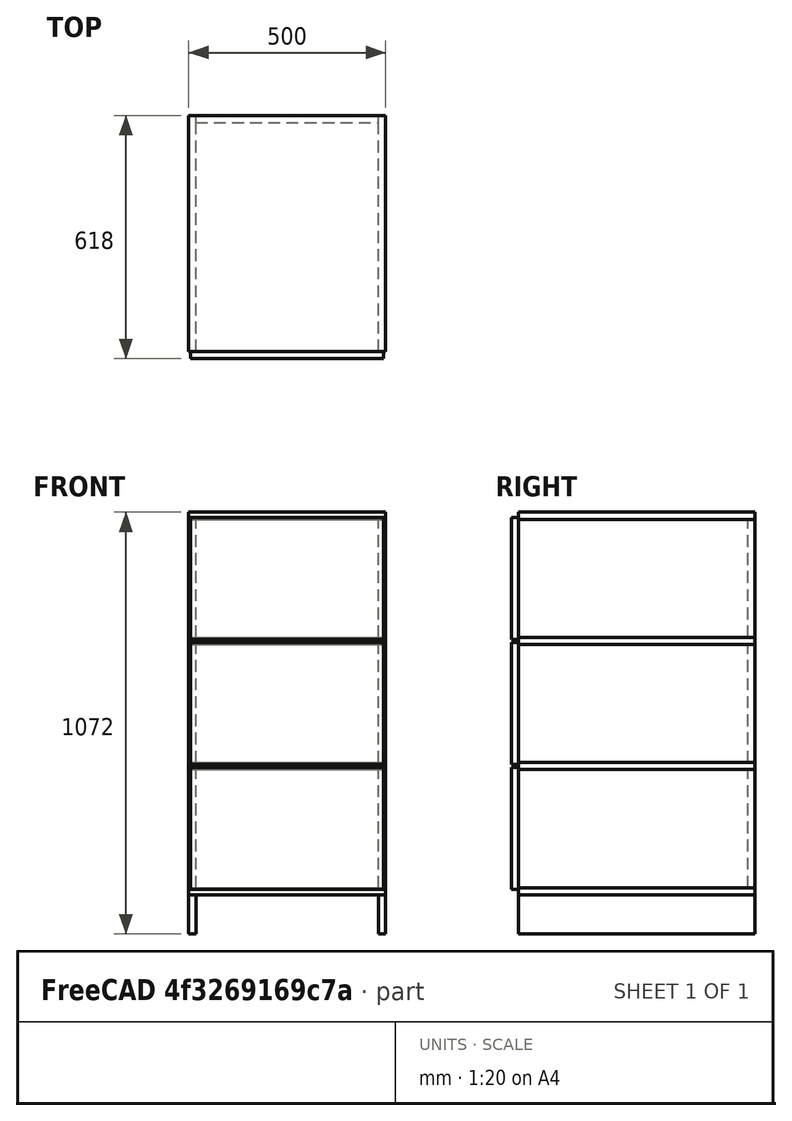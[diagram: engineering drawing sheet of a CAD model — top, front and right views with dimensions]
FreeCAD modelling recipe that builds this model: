
FCSTD DOCUMENT  (FreeCAD 0.21R33771 (Git))
Label: Test002_edgeband
License: All rights reserved
LicenseURL: http://en.wikipedia.org/wiki/All_rights_reserved
objects: Part::Box×18, App::DocumentObjectGroup×7, Spreadsheet::Sheet×1, TechDraw::DrawSVGTemplate×1, TechDraw::DrawViewSpreadsheet×1, TechDraw::DrawPage×1
note: 18 computed .brp shape members not serialized (recipe doc carries the construction recipe); baked Part::Feature solids carry a one-line shape summary decoded from their .brp

FEATURE [Part::Box] Box006  label="Foot L"
  AttacherType = Attacher::AttachEngine3D
  Height = 100
  Length = 18
  Width = 600
FEATURE [Part::Box] Box007  label="Side L1"
  AttacherType = Attacher::AttachEngine3D
  Height = 300
  Length = 18
  Placement = pos=(0,0,118) rot=(0,0,1;0rad)
  Width = 600
FEATURE [Part::Box] Box008  label="Side L2"
  AttacherType = Attacher::AttachEngine3D
  Height = 300
  Length = 18
  Placement = pos=(0,0,436) rot=(0,0,1;0rad)
  Width = 600
FEATURE [Part::Box] Box009  label="Side L3"
  AttacherType = Attacher::AttachEngine3D
  Height = 300
  Length = 18
  Placement = pos=(0,0,754) rot=(0,0,1;0rad)
  Width = 600
FEATURE [Part::Box] Box010  label="Foot R"
  AttacherType = Attacher::AttachEngine3D
  Height = 100
  Length = 18
  Placement = pos=(482,0,0) rot=(0,0,1;0rad)
  Width = 600
FEATURE [Part::Box] Box011  label="Side R1"
  AttacherType = Attacher::AttachEngine3D
  Height = 300
  Length = 18
  Placement = pos=(482,0,118) rot=(0,0,1;0rad)
  Width = 600
FEATURE [Part::Box] Box012  label="Side R2"
  AttacherType = Attacher::AttachEngine3D
  Height = 300
  Length = 18
  Placement = pos=(482,0,436) rot=(0,0,1;0rad)
  Width = 600
FEATURE [Part::Box] Box013  label="Side R3"
  AttacherType = Attacher::AttachEngine3D
  Height = 300
  Length = 18
  Placement = pos=(482,0,754) rot=(0,0,1;0rad)
  Width = 600
FEATURE [Part::Box] Box018  label="Back 1"
  AttacherType = Attacher::AttachEngine3D
  Height = 300
  Length = 464
  Placement = pos=(18,582,118) rot=(0,0,1;0rad)
  Width = 18
FEATURE [Part::Box] Box019  label="Back 2"
  AttacherType = Attacher::AttachEngine3D
  Height = 300
  Length = 464
  Placement = pos=(18,582,436) rot=(0,0,1;0rad)
  Width = 18
FEATURE [Part::Box] Box020  label="Back 3"
  AttacherType = Attacher::AttachEngine3D
  Height = 300
  Length = 464
  Placement = pos=(18,582,754) rot=(0,0,1;0rad)
  Width = 18
FEATURE [Part::Box] Box023  label="Top 1"
  AttacherType = Attacher::AttachEngine3D
  Height = 18
  Length = 500
  Placement = pos=(0,0,100) rot=(0,0,1;0rad)
  Width = 600
FEATURE [Part::Box] Box024  label="Top 2"
  AttacherType = Attacher::AttachEngine3D
  Height = 18
  Length = 500
  Placement = pos=(0,0,418) rot=(0,0,1;0rad)
  Width = 600
FEATURE [Part::Box] Box025  label="Top 3"
  AttacherType = Attacher::AttachEngine3D
  Height = 18
  Length = 500
  Placement = pos=(0,0,736) rot=(0,0,1;0rad)
  Width = 600
FEATURE [Part::Box] Box026  label="Top 4"
  AttacherType = Attacher::AttachEngine3D
  Height = 18
  Length = 500
  Placement = pos=(0,0,1054) rot=(0,0,1;0rad)
  Width = 600
FEATURE [Part::Box] Box027  label="Front 1"
  AttacherType = Attacher::AttachEngine3D
  Height = 310
  Length = 490
  Placement = pos=(5,-18,113) rot=(0,0,1;0rad)
  Width = 18
FEATURE [Part::Box] Box028  label="Front 2"
  AttacherType = Attacher::AttachEngine3D
  Height = 310
  Length = 490
  Placement = pos=(5,-18,431) rot=(0,0,1;0rad)
  Width = 18
FEATURE [Part::Box] Box029  label="Front 3"
  AttacherType = Attacher::AttachEngine3D
  Height = 310
  Length = 490
  Placement = pos=(5,-18,749) rot=(0,0,1;0rad)
  Width = 18
FEATURE [App::DocumentObjectGroup] Group006  label="Front"
  Group = -> [Box027,Box028,Box029]
FEATURE [App::DocumentObjectGroup] Group005  label="Top"
  Group = -> [Box023,Box024,Box025,Box026]
FEATURE [App::DocumentObjectGroup] Group004  label="Back"
  Group = -> [Box018,Box019,Box020]
FEATURE [App::DocumentObjectGroup] Group003  label="Side"
  Group = -> [Box007,Box008,Box009,Box011,Box012,Box013]
FEATURE [App::DocumentObjectGroup] Group007  label="Foot"
  Group = -> [Box006,Box010]
FEATURE [App::DocumentObjectGroup] Group002  label="White"
  Group = -> [Group003,Group004,Group005,Group006,Group007]
FEATURE [App::DocumentObjectGroup] Group001  label="Parts"
  Group = -> [Group002]
FEATURE [Spreadsheet::Sheet] toCut
  cells = A1='Name; B1='Dimensions; E1='Thickness; F1='Quantity; G1='m2; A2='Foot L; B2='100 mm; C2='x; D2='600 mm; E2='18 mm; F2=1; G2='0.06; A3=5; B3=6; D3=1; E3=2; F3=3; G3=4; A4='edge; F4='edge; G4='edge; A5='600 mm; F5='100 mm; G5='100 mm; A6='black; F6='black; G6='black; A8='Name; B8='Dimensions; E8='Thickness; F8='Quantity; G8='m2; A9='Side L1; B9='300 mm; C9='x; D9='600 mm; E9='18 mm; F9=1; G9='0.18; A10=5; B10=6; D10=1; E10=2; F10=3; G10=4; F11='edge; G11='edge; F12='300 mm; G12='300 mm; F13='black; G13='black; A15='Name; B15='Dimensions; E15='Thickness; F15='Quantity; G15='m2; A16='Side L2; B16='300 mm; C16='x; D16='600 mm; E16='18 mm; F16=1; G16='0.18; A17=5; B17=6; D17=1; E17=2; F17=3; G17=4; F18='edge; G18='edge; F19='300 mm; G19='300 mm; F20='black; G20='black; A22='Name; B22='Dimensions; E22='Thickness; F22='Quantity; G22='m2; A23='Side L3; B23='300 mm; C23='x; D23='600 mm; E23='18 mm; F23=1; G23='0.18; A24=5; B24=6; D24=1; E24=2; F24=3; G24=4; F25='edge; G25='edge; F26='300 mm; G26='300 mm; F27='black; G27='black; A29='Name; B29='Dimensions; E29='Thickness; F29='Quantity; G29='m2; A30='Foot R; B30='100 mm; C30='x; D30='600 mm; E30='18 mm; F30=1; G30='0.06; A31=5; B31=6; D31=1; E31=2; F31=3; G31=4; A32='edge; F32='edge; G32='edge; A33='600 mm; F33='100 mm; G33='100 mm; A34='black; F34='black; G34='black; A36='Name; B36='Dimensions; E36='Thickness; F36='Quantity; G36='m2; A37='Side R1; B37='300 mm; C37='x; D37='600 mm; E37='18 mm; F37=1; G37='0.18; A38=5; B38=6; D38=1; E38=2; F38=3; G38=4; F39='edge; G39='edge; F40='300 mm; G40='300 mm; F41='black; G41='black; A43='Name; B43='Dimensions; E43='Thickness; F43='Quantity; G43='m2; A44='Side R2; B44='300 mm; C44='x; D44='600 mm; E44='18 mm; F44=1; G44='0.18; A45=5; B45=6; D45=1; E45=2; F45=3; G45=4; F46='edge; G46='edge; F47='300 mm; G47='300 mm; F48='black; G48='black; A50='Name; B50='Dimensions; E50='Thickness; F50='Quantity; G50='m2; A51='Side R3; B51='300 mm; C51='x; D51='600 mm; E51='18 mm; F51=1; G51='0.18; A52=5; B52=6; D52=1; E52=2; F52=3; G52=4; F53='edge; G53='edge; F54='300 mm; G54='300 mm; F55='black; G55='black; A57='Name; B57='Dimensions; +258 more cells
FEATURE [TechDraw::DrawSVGTemplate] Template
  Height = 297
  Orientation = 0
  Template = <path>
  Width = 210
FEATURE [TechDraw::DrawViewSpreadsheet] Sheet
  CellEnd = G123
  CellStart = A1
  Font = DejaVu Sans
  LineWidth = 0.1
  LockPosition = false
  Rotation = 0
  ScaleType = 2
  Source = -> toCut
  Symbol = <blob: 157970 chars omitted>
  TextSize = 13
  X = 105
  Y = 148
FEATURE [TechDraw::DrawPage] toPrint
  KeepUpdated = true
  NextBalloonIndex = 1
  ProjectionType = 0
  Template = -> Template
  Views = -> [Sheet]
note: 1 file-system path scrubbed to <path> (originals preserved in the JSON sidecar)
